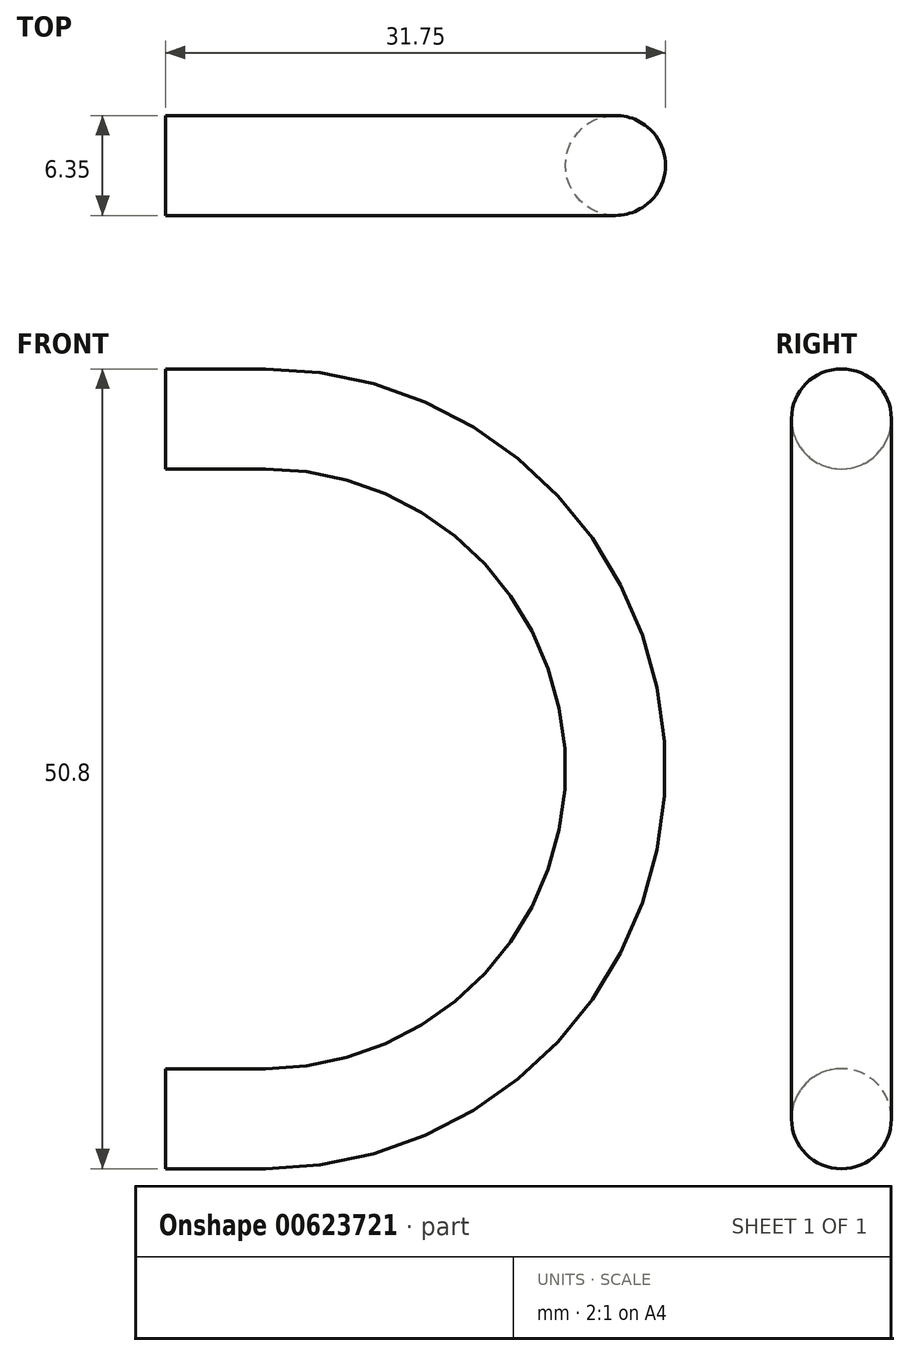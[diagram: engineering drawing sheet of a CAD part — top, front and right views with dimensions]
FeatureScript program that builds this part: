
annotation { "Feature Type Name" : "Feature", "Feature Type Description" : "" }
export const myFeature = defineFeature(function(context is Context, id is Id, definition is map)
    precondition{}
    {
        {
            var Q0;
            Q0=qCreatedBy(makeId("Front.planeOp"),FACE);
            var sketch = newSketch(context, id + "F0", { "sketchPlane" : qUnion([Q0])});
            skLineSegment(sketch, "E0", {"start": v(0, 0) * mm, "end": v(0, 6.35) * mm});
            skPoint(sketch, "E1.endSnap0", {"position": v(0, 25.4) * mm});
            skLineSegment(sketch, "E2", {"start": v(0, 50.8) * mm, "end": v(6.35, 50.8) * mm});
            skLineSegment(sketch, "E3", {"start": v(0, 0) * mm, "end": v(6.35, 0) * mm});
            skArc(sketch, "E4", {"start": v(6.35, 0) * mm, "mid": v(31.75, 25.4) * mm, "end": v(6.35, 50.8) * mm});
            skLineSegment(sketch, "E5.0", {"start": v(0, 44.45) * mm, "end": v(6.35, 44.45) * mm});
            skArc(sketch, "E5.1", {"start": v(6.35, 6.35) * mm, "mid": v(25.4, 25.4) * mm, "end": v(6.35, 44.45) * mm});
            skLineSegment(sketch, "E5.2", {"start": v(0, 6.35) * mm, "end": v(6.35, 6.35) * mm});
            skLineSegment(sketch, "E6.trimOffspring", {"start": v(0, 44.45) * mm, "end": v(0, 50.8) * mm});
            skSolve(sketch);
        }
        {
            var Q0;
            Q0=makeQuery(id+"F0.imprint","IMPRINT",FACE,{"disambiguationData":[TD([[makeQuery(id+"F0.imprint","IMPRINT",EDGE,{"derivedFrom":sQuery(id+"F0.wireOp",EDGE,"E0")}),-1.0]])]});
            extrude(context, id + "F1", {"entities" : qUnion([Q0]), "depth" : 6.35 * mm, "offsetDistance" : 25.4 * mm});
        }
        {
            var Q0;
            Q0=makeQuery(id+"F1.opExtrude","CAP_EDGE",EDGE,{"disambiguationData":[OSD([sQuery(id+"F0.wireOp",EDGE,"E4")])],"isStart":false});
            var Q1;
            Q1=makeQuery(id+"F1.opExtrude","CAP_EDGE",EDGE,{"disambiguationData":[OSD([sQuery(id+"F0.wireOp",EDGE,"E5.1")])],"isStart":false});
            var Q2;
            Q2=makeQuery(id+"F1.opExtrude","CAP_EDGE",EDGE,{"disambiguationData":[OSD([sQuery(id+"F0.wireOp",EDGE,"E4")])],"isStart":true});
            var Q3;
            Q3=makeQuery(id+"F1.opExtrude","CAP_EDGE",EDGE,{"disambiguationData":[OSD([sQuery(id+"F0.wireOp",EDGE,"E5.2")])],"isStart":true});
            fillet(context, id + "F2", {"entities" : qUnion([Q0, Q1, Q2, Q3]), "radius" : 3.17 * mm, "tangentPropagation" : true, "allowEdgeOverflow" : false});
        }
    });
